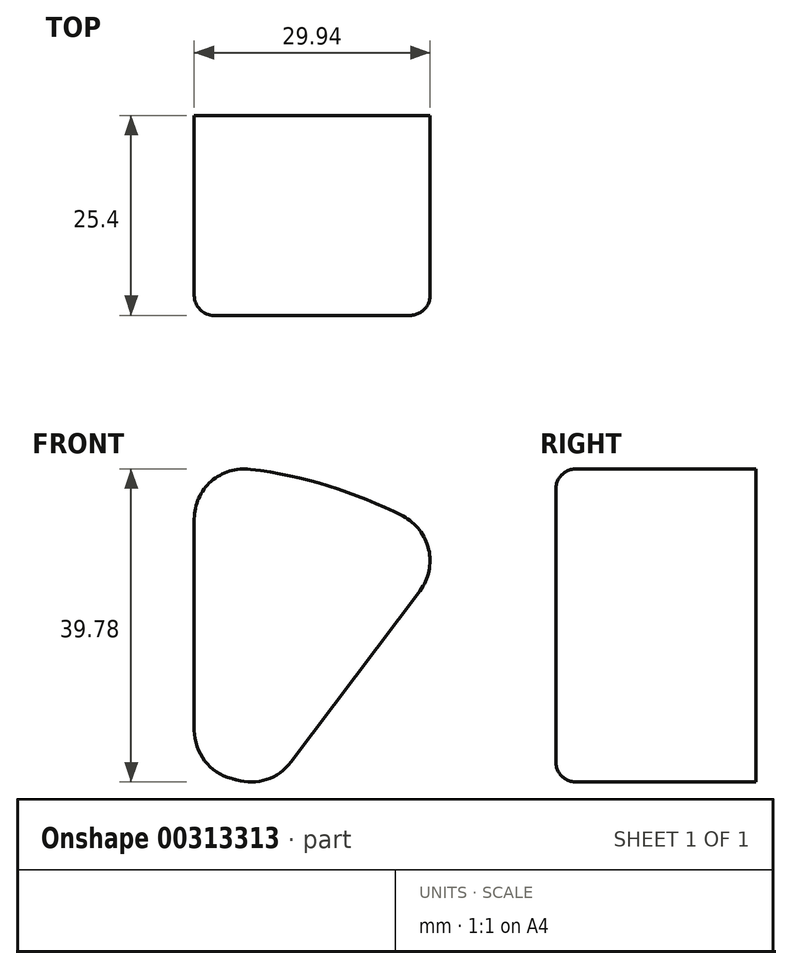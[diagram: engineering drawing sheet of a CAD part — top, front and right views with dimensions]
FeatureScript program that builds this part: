
annotation { "Feature Type Name" : "Feature", "Feature Type Description" : "" }
export const myFeature = defineFeature(function(context is Context, id is Id, definition is map)
    precondition{}
    {
        {
            var Q0;
            Q0=qCreatedBy(makeId("Front.planeOp"),FACE);
            var sketch = newSketch(context, id + "F0", { "sketchPlane" : qUnion([Q0])});
            skCircle(sketch, "E0", {"center": v(0, 0) * mm, "radius": 66.74 * mm});
            skSolve(sketch);
        }
        {
            var Q0;
            Q0=makeQuery(id+"F0.imprint","IMPRINT",FACE,{"disambiguationData":[TD([[makeQuery(id+"F0.imprint","IMPRINT",EDGE,{"derivedFrom":sQuery(id+"F0.wireOp",EDGE,"E0")}),1.0]])]});
            extrude(context, id + "F1", {"entities" : qUnion([Q0]), "depth" : 25.4 * mm});
        }
        {
            var Q0;
            Q0=makeQuery(id+"F1.opExtrude","CAP_FACE",FACE,{"disambiguationData":[OSD([sQuery(id+"F0.wireOp",EDGE,"E0")])],"isStart":false});
            var sketch = newSketch(context, id + "F2", { "sketchPlane" : qUnion([Q0])});
            skArc(sketch, "E1", {"start": v(7.13, 57.55) * mm, "mid": v(17.07, 55.42) * mm, "end": v(26.5, 51.58) * mm});
            skArc(sketch, "E2", {"start": v(4.75, 18.25) * mm, "mid": v(5.07, 18.17) * mm, "end": v(5.39, 18.07) * mm});
            skLineSegment(sketch, "E3", {"start": v(0, 51.24) * mm, "end": v(0, 24.4) * mm});
            skLineSegment(sketch, "E4", {"start": v(28.66, 42.11) * mm, "end": v(12.27, 20.34) * mm});
            skPoint(sketch, "E5.visualSharp", {"position": v(0, 57.99) * mm});
            skArc(sketch, "E5.filletArc", {"start": v(7.13, 57.55) * mm, "mid": v(2.15, 56) * mm, "end": v(0, 51.24) * mm});
            skPoint(sketch, "E6.visualSharp", {"position": v(32.9, 47.75) * mm});
            skArc(sketch, "E6.filletArc", {"start": v(28.66, 42.11) * mm, "mid": v(29.78, 47.35) * mm, "end": v(26.5, 51.58) * mm});
            skPoint(sketch, "E7.visualSharp", {"position": v(0, 18.86) * mm});
            skArc(sketch, "E7.filletArc", {"start": v(0, 24.4) * mm, "mid": v(1.33, 20.51) * mm, "end": v(4.75, 18.25) * mm});
            skPoint(sketch, "E8.visualSharp", {"position": v(9.3, 16.4) * mm});
            skArc(sketch, "E8.filletArc", {"start": v(5.39, 18.07) * mm, "mid": v(9.18, 18.13) * mm, "end": v(12.27, 20.34) * mm});
            skSolve(sketch);
        }
        {
            var Q0;
            Q0=makeQuery(id+"F2.imprint","IMPRINT",FACE,{"disambiguationData":[TD([[makeQuery(id+"F2.imprint","IMPRINT",EDGE,{"derivedFrom":sQuery(id+"F2.wireOp",EDGE,"E1")}),-1.0]])]});
            extrude(context, id + "F3", {"entities" : qUnion([Q0]), "operationType" : NewBodyOperationType.REMOVE, "oppositeDirection" : true, "depth" : 25.4 * mm});
        }
        {
            var Q0;
            Q0=makeQuery(id+"F1.opExtrude","CAP_FACE",FACE,{"disambiguationData":[OSD([sQuery(id+"F0.wireOp",EDGE,"E0")])],"isStart":false});
            fillet(context, id + "F4", {"entities" : qUnion([Q0]), "radius" : 2.54 * mm, "tangentPropagation" : true, "allowEdgeOverflow" : false});
        }
    });
